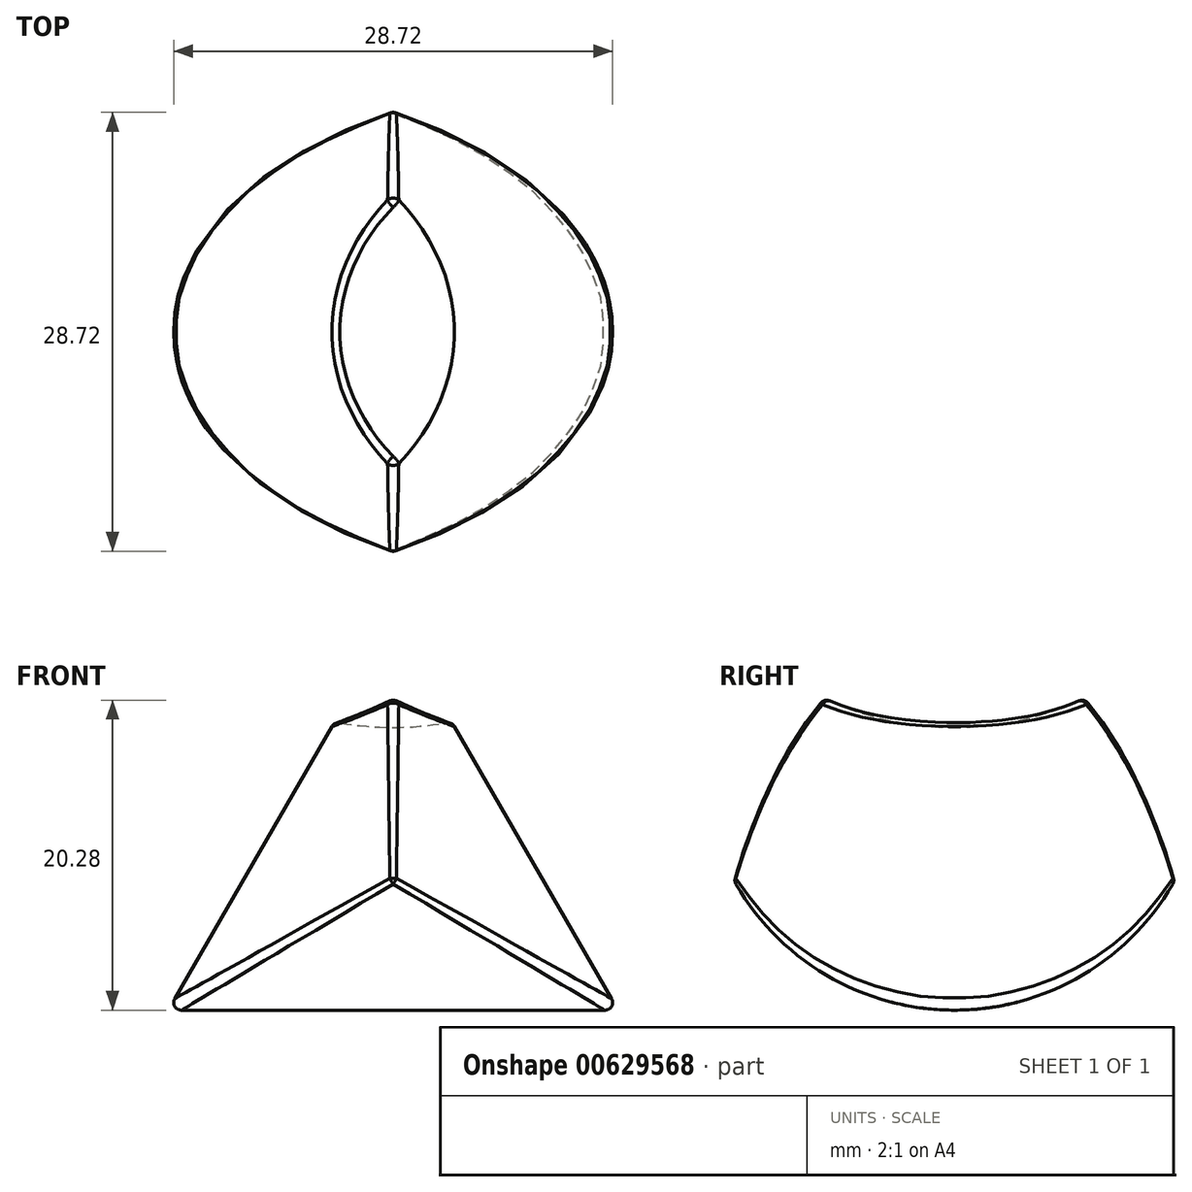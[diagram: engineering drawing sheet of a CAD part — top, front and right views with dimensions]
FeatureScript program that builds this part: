
annotation { "Feature Type Name" : "Feature", "Feature Type Description" : "" }
export const myFeature = defineFeature(function(context is Context, id is Id, definition is map)
    precondition{}
    {
        {
            var Q0;
            Q0=qCreatedBy(makeId("Front.planeOp"),FACE);
            var sketch = newSketch(context, id + "F0", { "sketchPlane" : qUnion([Q0])});
            skCircle(sketch, "E0.cCircle", {"center": v(0, 25) * mm, "radius": 25 * mm, "construction": true});
            skLineSegment(sketch, "E0.0", {"start": v(0, 75) * mm, "end": v(43.3, 0) * mm});
            skLineSegment(sketch, "E0.1", {"start": v(43.3, 0) * mm, "end": v(-43.3, 0) * mm});
            skLineSegment(sketch, "E0.2", {"start": v(-43.3, 0) * mm, "end": v(0, 75) * mm});
            skPoint(sketch, "E0.0.midPoint", {"position": v(21.65, 37.5) * mm});
            skSolve(sketch);
        }
        {
            var Q0;
            Q0=makeQuery(id+"F0.imprint","IMPRINT",FACE,{"disambiguationData":[TD([[makeQuery(id+"F0.imprint","IMPRINT",EDGE,{"derivedFrom":sQuery(id+"F0.wireOp",EDGE,"E0.0")}),-1.0]])]});
            extrude(context, id + "F1", {"entities" : qUnion([Q0]), "depth" : 25 * mm, "offsetDistance" : 25 * mm, "hasDraft" : true, "draftAngle" : 60 * degree, "draftPullDirection" : true});
        }
        {
            var Q0;
            Q0=makeQuery(id+"F1.opExtrude","CAP_FACE",FACE,{"disambiguationData":[OSD([sQuery(id+"F0.wireOp",EDGE,"E0.0"),sQuery(id+"F0.wireOp",EDGE,"E0.1"),sQuery(id+"F0.wireOp",EDGE,"E0.2")])],"isStart":true});
            extrude(context, id + "F2", {"entities" : qUnion([Q0]), "operationType" : NewBodyOperationType.ADD, "depth" : 25 * mm, "offsetDistance" : 25 * mm, "hasDraft" : true, "draftAngle" : 60 * degree, "draftPullDirection" : true});
        }
        {
            var Q0;
            {var subQ0=sQuery(id+"F0.wireOp",EDGE,"E0.0");Q0=makeQuery(id+"F2.boolean.opBoolean","MERGE",EDGE,{"derivedFrom":[makeQuery(id+"F1.opExtrude","CAP_EDGE",EDGE,{"disambiguationData":[OSD([subQ0])],"isStart":true}),makeQuery(id+"F2.opExtrude","CAP_EDGE",EDGE,{"disambiguationData":[OSD([subQ0])],"isStart":true})]});}
            var Q1;
            {var subQ0=sQuery(id+"F0.wireOp",EDGE,"E0.1");Q1=makeQuery(id+"F2.boolean.opBoolean","MERGE",EDGE,{"derivedFrom":[makeQuery(id+"F1.opExtrude","CAP_EDGE",EDGE,{"disambiguationData":[OSD([subQ0])],"isStart":true}),makeQuery(id+"F2.opExtrude","CAP_EDGE",EDGE,{"disambiguationData":[OSD([subQ0])],"isStart":true})]});}
            var Q2;
            {var subQ0=sQuery(id+"F0.wireOp",EDGE,"E0.2");Q2=makeQuery(id+"F2.boolean.opBoolean","MERGE",EDGE,{"derivedFrom":[makeQuery(id+"F1.opExtrude","CAP_EDGE",EDGE,{"disambiguationData":[OSD([subQ0])],"isStart":true}),makeQuery(id+"F2.opExtrude","CAP_EDGE",EDGE,{"disambiguationData":[OSD([subQ0])],"isStart":true})]});}
            fillet(context, id + "F3", {"entities" : qUnion([Q0, Q1, Q2]), "radius" : 16.5 * mm, "tangentPropagation" : true, "allowEdgeOverflow" : false});
        }
        {
            var Q0;
            Q0=qCreatedBy(makeId("Right.planeOp"),FACE);
            var sketch = newSketch(context, id + "F4", { "sketchPlane" : qUnion([Q0])});
            skArc(sketch, "E1", {"start": v(-18.75, 48.04) * mm, "mid": v(0, 35) * mm, "end": v(18.75, 48.04) * mm});
            skLineSegment(sketch, "E2", {"start": v(-18.75, 48.04) * mm, "end": v(18.75, 48.04) * mm});
            skLineSegment(sketch, "E3", {"start": v(0, 55) * mm, "end": v(-18.78, 55) * mm, "construction": true});
            skSolve(sketch);
        }
        {
            var Q0;
            Q0=makeQuery(id+"F4.imprint","IMPRINT",FACE,{"disambiguationData":[TD([[makeQuery(id+"F4.imprint","IMPRINT",EDGE,{"derivedFrom":sQuery(id+"F4.wireOp",EDGE,"E1")}),1.0]])]});
            var Q1;
            Q1=sQuery(id+"F4.wireOp",EDGE,"E3");
            revolve(context, id + "F5", {"operationType" : NewBodyOperationType.REMOVE, "entities" : qUnion([Q0]), "axis" : qUnion([Q1]), "revolveType" : RevolveType.FULL, "oppositeDirection" : true});
        }
        {
            var Q0;
            Q0=qCreatedBy(makeId("Right.planeOp"),FACE);
            var sketch = newSketch(context, id + "F6", { "sketchPlane" : qUnion([Q0])});
            skPoint(sketch, "E4.0", {"position": v(14.43, 25) * mm});
            skLineSegment(sketch, "E5", {"start": v(14.43, 25) * mm, "end": v(21.23, 25) * mm, "construction": true});
            skSolve(sketch);
        }
        {
            var Q0;
            Q0=makeQuery(id+"F3.opFillet","BLEND_FACE",FACE,{"disambiguationData":[OSD([sQuery(id+"F0.wireOp",EDGE,"E0.0")])]});
            var Q1;
            Q1=makeQuery(id+"F1.opExtrude","SWEPT_EDGE",EDGE,{"disambiguationData":[OSD([sQuery(id+"F0.wireOp",EDGE,"E0.0"),sQuery(id+"F0.wireOp",EDGE,"E0.1")])]});
            var Q2;
            Q2=makeQuery(id+"F1.opExtrude","SWEPT_EDGE",EDGE,{"disambiguationData":[OSD([sQuery(id+"F0.wireOp",EDGE,"E0.0"),sQuery(id+"F0.wireOp",EDGE,"E0.2")])]});
            var Q3;
            Q3=makeQuery(id+"F1.opExtrude","SWEPT_EDGE",EDGE,{"disambiguationData":[OSD([sQuery(id+"F0.wireOp",EDGE,"E0.1"),sQuery(id+"F0.wireOp",EDGE,"E0.2")])]});
            var Q4;
            {var subQ0=sQuery(id+"F0.wireOp",EDGE,"E0.2");Q4=makeQuery(id+"F3.opFillet","BLEND_EDGE",EDGE,{"blendedFrom":[makeQuery(id+"F2.boolean.opBoolean","MERGE",EDGE,{"derivedFrom":[makeQuery(id+"F1.opExtrude","CAP_EDGE",EDGE,{"disambiguationData":[OSD([subQ0])],"isStart":true}),makeQuery(id+"F2.opExtrude","CAP_EDGE",EDGE,{"disambiguationData":[OSD([subQ0])],"isStart":true})]}),makeQuery(id+"F1.opExtrude","SWEPT_FACE",FACE,{"disambiguationData":[OSD([subQ0])]})],"blendedInto":[makeQuery(id+"F1.opExtrude","SWEPT_FACE",FACE,{"disambiguationData":[OSD([subQ0])]})]});}
            var Q5;
            {var subQ0=sQuery(id+"F0.wireOp",EDGE,"E0.1");Q5=makeQuery(id+"F3.opFillet","BLEND_EDGE",EDGE,{"blendedFrom":[makeQuery(id+"F2.boolean.opBoolean","MERGE",EDGE,{"derivedFrom":[makeQuery(id+"F1.opExtrude","CAP_EDGE",EDGE,{"disambiguationData":[OSD([subQ0])],"isStart":true}),makeQuery(id+"F2.opExtrude","CAP_EDGE",EDGE,{"disambiguationData":[OSD([subQ0])],"isStart":true})]}),makeQuery(id+"F1.opExtrude","SWEPT_FACE",FACE,{"disambiguationData":[OSD([subQ0])]})],"blendedInto":[makeQuery(id+"F1.opExtrude","SWEPT_FACE",FACE,{"disambiguationData":[OSD([subQ0])]})]});}
            var Q6;
            Q6=makeQuery(id+"F3.opFillet","BLEND_FACE",FACE,{"disambiguationData":[OSD([sQuery(id+"F0.wireOp",EDGE,"E0.1")])]});
            var Q7;
            Q7=makeQuery(id+"F3.opFillet","BLEND_FACE",FACE,{"disambiguationData":[OSD([sQuery(id+"F0.wireOp",EDGE,"E0.2")])]});
            var Q8;
            Q8=makeQuery(id+"F2.opExtrude","SWEPT_FACE",FACE,{"disambiguationData":[OSD([sQuery(id+"F0.wireOp",EDGE,"E0.2")])]});
            var Q9;
            {var subQ0=sQuery(id+"F0.wireOp",EDGE,"E0.0");Q9=makeQuery(id+"F3.opFillet","BLEND_EDGE",EDGE,{"blendedFrom":[makeQuery(id+"F2.boolean.opBoolean","MERGE",EDGE,{"derivedFrom":[makeQuery(id+"F1.opExtrude","CAP_EDGE",EDGE,{"disambiguationData":[OSD([subQ0])],"isStart":true}),makeQuery(id+"F2.opExtrude","CAP_EDGE",EDGE,{"disambiguationData":[OSD([subQ0])],"isStart":true})]}),makeQuery(id+"F2.opExtrude","SWEPT_FACE",FACE,{"disambiguationData":[OSD([subQ0])]})],"blendedInto":[makeQuery(id+"F2.opExtrude","SWEPT_FACE",FACE,{"disambiguationData":[OSD([subQ0])]})]});}
            var Q10;
            Q10=makeQuery(id+"F2.opExtrude","SWEPT_EDGE",EDGE,{"disambiguationData":[OSD([sQuery(id+"F0.wireOp",EDGE,"E0.1"),sQuery(id+"F0.wireOp",EDGE,"E0.2")])]});
            var Q11;
            {var subQ0=sQuery(id+"F0.wireOp",EDGE,"E0.1");Q11=makeQuery(id+"F3.opFillet","BLEND_EDGE",EDGE,{"blendedFrom":[makeQuery(id+"F2.boolean.opBoolean","MERGE",EDGE,{"derivedFrom":[makeQuery(id+"F1.opExtrude","CAP_EDGE",EDGE,{"disambiguationData":[OSD([subQ0])],"isStart":true}),makeQuery(id+"F2.opExtrude","CAP_EDGE",EDGE,{"disambiguationData":[OSD([subQ0])],"isStart":true})]}),makeQuery(id+"F2.opExtrude","SWEPT_FACE",FACE,{"disambiguationData":[OSD([subQ0])]})],"blendedInto":[makeQuery(id+"F2.opExtrude","SWEPT_FACE",FACE,{"disambiguationData":[OSD([subQ0])]})]});}
            var Q12;
            {var subQ0=sQuery(id+"F0.wireOp",EDGE,"E0.2");Q12=makeQuery(id+"F3.opFillet","BLEND_EDGE",EDGE,{"blendedFrom":[makeQuery(id+"F2.boolean.opBoolean","MERGE",EDGE,{"derivedFrom":[makeQuery(id+"F1.opExtrude","CAP_EDGE",EDGE,{"disambiguationData":[OSD([subQ0])],"isStart":true}),makeQuery(id+"F2.opExtrude","CAP_EDGE",EDGE,{"disambiguationData":[OSD([subQ0])],"isStart":true})]}),makeQuery(id+"F2.opExtrude","SWEPT_FACE",FACE,{"disambiguationData":[OSD([subQ0])]})],"blendedInto":[makeQuery(id+"F2.opExtrude","SWEPT_FACE",FACE,{"disambiguationData":[OSD([subQ0])]})]});}
            var Q13;
            Q13=makeQuery(id+"F2.opExtrude","SWEPT_EDGE",EDGE,{"disambiguationData":[OSD([sQuery(id+"F0.wireOp",EDGE,"E0.0"),sQuery(id+"F0.wireOp",EDGE,"E0.2")])]});
            var Q14;
            Q14=makeQuery(id+"F2.opExtrude","SWEPT_EDGE",EDGE,{"disambiguationData":[OSD([sQuery(id+"F0.wireOp",EDGE,"E0.0"),sQuery(id+"F0.wireOp",EDGE,"E0.1")])]});
            fillet(context, id + "F7", {"entities" : qUnion([Q0, Q1, Q2, Q3, Q4, Q5, Q6, Q7, Q8, Q9, Q10, Q11, Q12, Q13, Q14]), "radius" : .5 * mm, "tangentPropagation" : true, "allowEdgeOverflow" : false});
        }
    });
